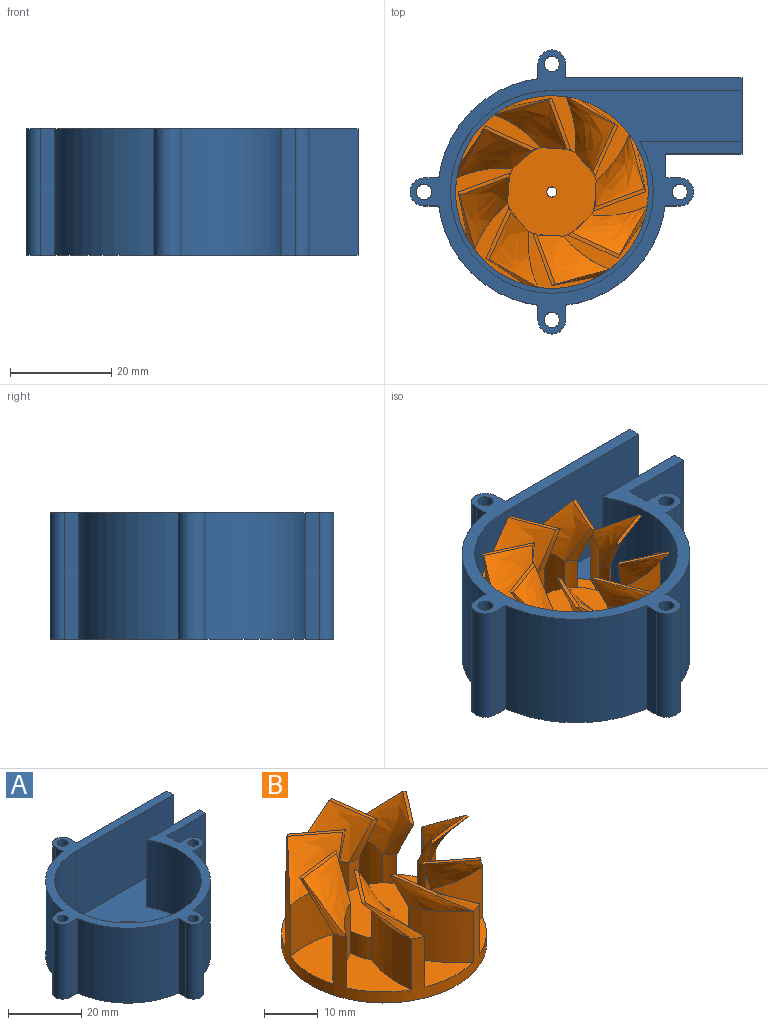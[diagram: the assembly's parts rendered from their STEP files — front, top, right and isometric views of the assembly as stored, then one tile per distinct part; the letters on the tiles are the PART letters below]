
ASSEMBLY  parts=2 mates=1
PART A: 34 faces, bbox 65.5x56x25 mm
  f0: plane 25x2.59mm, normal (0,1,0), area 64.7mm2, adj f1,f25,f26,f27
  f1: plane 25x4.75mm, normal (1,0,0), area 118.9mm2, adj f0,f2,f26,f27
  f2: plane 25x15mm, normal (0,-1,0), area 375mm2, adj f1,f6,f26,f27
  f3: plane 22.5x20.18mm, normal (0,1,0), area 454mm2, adj f4,f6,f26,f28
  f4: cylinder r=20mm len=40mm, axis (0,0,-1), area 2356.2mm2, adj f3,f5,f26,f28
  f5: plane 37.5x22.5mm, normal (0,-1,0), area 843.8mm2, adj f4,f6,f26,f28
  f6: plane 25x15mm, normal (1,0,0), area 150mm2, adj f2,f3,f5,f7,f26,f27,f28
  f7: plane 34.75x25mm, normal (0,1,0), area 868.9mm2, adj f6,f8,f26,f27
  f8: plane 25x2.59mm, normal (1,0,0), area 64.7mm2, adj f7,f9,f26,f27
  f9: cylinder r=2.75mm len=25mm, axis (0,0,-1), area 224mm2, adj f8,f10,f26,f27
  f10: plane 25x2.76mm, normal (-1,0,0), area 68.9mm2, adj f9,f11,f26,f27
  f11: cylinder r=22.5mm len=25mm, axis (0,0,-1), area 746mm2, adj f10,f12,f26,f27
  f12: plane 25x2.76mm, normal (0,1,0), area 68.9mm2, adj f11,f13,f26,f27
  f13: cylinder r=2.75mm len=25mm, axis (0,0,-1), area 224mm2, adj f12,f14,f26,f27
  f14: plane 25x2.76mm, normal (0,-1,0), area 68.9mm2, adj f13,f15,f26,f27
  f15: cylinder r=22.5mm len=25mm, axis (0,0,-1), area 746mm2, adj f14,f16,f26,f27
  f16: plane 25x2.76mm, normal (-1,0,0), area 68.9mm2, adj f15,f17,f26,f27
  f17: cylinder r=2.75mm len=25mm, axis (0,0,-1), area 224mm2, adj f16,f18,f26,f27
  f18: plane 25x2.76mm, normal (1,0,0), area 68.9mm2, adj f17,f19,f26,f27
  f19: cylinder r=22.5mm len=25mm, axis (0,0,-1), area 746mm2, adj f18,f20,f26,f27
  f20: plane 25x2.76mm, normal (0,-1,0), area 68.9mm2, adj f19,f25,f26,f27
  f21: cylinder r=1.5mm len=25mm, axis (0,0,-1), area 235.6mm2, adj f26,f27
  f22: cylinder r=1.5mm len=25mm, axis (0,0,-1), area 235.6mm2, adj f26,f27
  f23: cylinder r=1.5mm len=25mm, axis (0,0,-1), area 235.6mm2, adj f26,f27
  f24: cylinder r=1.5mm len=25mm, axis (0,0,-1), area 235.6mm2, adj f26,f27
  f25: cylinder r=2.75mm len=25mm, axis (0,0,-1), area 224mm2, adj f0,f20,f26,f27
  f26: plane 65.5x56mm, normal (0,0,1), area 495.8mm2, adj f0,f1,f2,f3,f4,f5,f6,f7
  f27: plane 65.5x56mm, normal (0,0,-1), area 1985mm2, adj f0,f1,f2,f6,f7,f8,f9,f10
  f28: plane 57.5x40mm, normal (0,0,1), area 1354.9mm2, adj f3,f4,f5,f6,f30
  f29: cylinder r=5mm len=10mm, axis (0,0,-1), area 125.7mm2, adj f31,f33
  f30: cylinder r=7mm len=14mm, axis (0,0,-1), area 175.9mm2, adj f28,f31
  f31: plane 14x14mm, normal (0,0,1), area 75.4mm2, adj f29,f30
  f32: cylinder r=2.5mm len=5mm, axis (0,0,-1), area 39.3mm2, adj f27,f33
  f33: plane 10x10mm, normal (0,0,1), area 58.9mm2, adj f29,f32
PART B: 88 faces, bbox 38x38x22 mm
  f0: cylinder r=9mm len=5mm, axis (0,0,-1), area 22.6mm2, adj f3,f19,f43,f47
  f1: plane 12.48x12.46mm, normal (0,0,1), area 84.3mm2, adj f14,f17,f26,f46
  f2: cylinder r=9mm len=5mm, axis (0,0,-1), area 22.6mm2, adj f5,f19,f40,f44
  f3: plane 16.31x9.64mm, normal (0,0,1), area 84.3mm2, adj f0,f17,f43,f47
  f4: cylinder r=9mm len=5mm, axis (0,0,-1), area 22.6mm2, adj f7,f19,f37,f41
  f5: plane 12.48x12.46mm, normal (0,0,1), area 84.3mm2, adj f2,f17,f40,f44
  f6: cylinder r=9mm len=5mm, axis (0,0,-1), area 22.6mm2, adj f9,f19,f34,f38
  f7: plane 16.31x9.64mm, normal (0,0,1), area 84.3mm2, adj f4,f17,f37,f41
  f8: cylinder r=9mm len=5mm, axis (0,0,-1), area 22.6mm2, adj f11,f19,f31,f35
  f9: plane 12.48x12.46mm, normal (0,0,1), area 84.3mm2, adj f6,f17,f34,f38
  f10: cylinder r=9mm len=5mm, axis (0,0,-1), area 22.6mm2, adj f13,f19,f28,f32
  f11: plane 16.31x9.64mm, normal (0,0,1), area 84.3mm2, adj f8,f17,f31,f35
  f12: cylinder r=9mm len=5mm, axis (0,0,-1), area 22.6mm2, adj f15,f19,f25,f29
  f13: plane 12.48x12.46mm, normal (0,0,1), area 84.3mm2, adj f10,f17,f28,f32
  f14: cylinder r=9mm len=5mm, axis (0,0,-1), area 22.6mm2, adj f1,f19,f26,f46
  f15: plane 16.31x9.64mm, normal (0,0,1), area 84.3mm2, adj f12,f17,f25,f29
  f16: cylinder r=7.5mm len=15mm, axis (0,0,-1), area 259.2mm2, adj f18,f20
  f17: cylinder r=19mm len=38mm, axis (0,0,-1), area 544.5mm2, adj f1,f3,f5,f7,f9,f11,f13,f15
  f18: plane 38x38mm, normal (0,0,-1), area 957.4mm2, adj f16,f17
  f19: plane 18x18mm, normal (0,0,1), area 251.3mm2, adj f0,f2,f4,f6,f8,f10,f12,f14
  f20: plane 15x15mm, normal (0,0,-1), area 113.1mm2, adj f16,f21
  f21: cylinder r=4.5mm len=9mm, axis (0,0,-1), area 155.5mm2, adj f20,f22
  f22: plane 9x9mm, normal (0,0,-1), area 60.5mm2, adj f21,f23
  f23: cylinder r=1mm len=7.5mm, axis (0,0,-1), area 47.1mm2, adj f19,f22
  f24: cylinder r=9mm len=6.5mm, axis (0,0,-1), area 16.5mm2, adj f19,f25,f26,f69
  f25: cylinder r=20.82mm len=11.5mm, axis (0,0,-1), area 130.3mm2, adj f12,f15,f17,f24,f72
  f26: cylinder r=23mm len=11.5mm, axis (0,0,-1), area 140.9mm2, adj f1,f14,f17,f24,f70
  f27: cylinder r=9mm len=6.5mm, axis (0,0,-1), area 16.5mm2, adj f19,f28,f29,f64
  f28: cylinder r=20.82mm len=11.5mm, axis (0,0,-1), area 130.3mm2, adj f10,f13,f17,f27,f67
  f29: cylinder r=23mm len=12mm, axis (0,0,-1), area 140.9mm2, adj f12,f15,f17,f27,f65
  f30: cylinder r=9mm len=6.5mm, axis (0,0,-1), area 16.5mm2, adj f19,f31,f32,f59
  f31: cylinder r=20.82mm len=11.5mm, axis (0,0,-1), area 130.3mm2, adj f8,f11,f17,f30,f62
  f32: cylinder r=23mm len=11.5mm, axis (0,0,-1), area 140.9mm2, adj f10,f13,f17,f30,f60
  f33: cylinder r=9mm len=6.5mm, axis (0,0,-1), area 16.5mm2, adj f19,f34,f35,f54
  f34: cylinder r=20.82mm len=11.5mm, axis (0,0,-1), area 130.3mm2, adj f6,f9,f17,f33,f57
  f35: cylinder r=23mm len=12mm, axis (0,0,-1), area 140.9mm2, adj f8,f11,f17,f33,f55
  f36: cylinder r=9mm len=6.5mm, axis (0,0,-1), area 16.5mm2, adj f19,f37,f38,f52
  f37: cylinder r=20.82mm len=11.5mm, axis (0,0,-1), area 130.3mm2, adj f4,f7,f17,f36,f51
  f38: cylinder r=23mm len=11.5mm, axis (0,0,-1), area 140.9mm2, adj f6,f9,f17,f36,f49
  f39: cylinder r=9mm len=6.5mm, axis (0,0,-1), area 16.5mm2, adj f19,f40,f41,f84
  f40: cylinder r=20.82mm len=11.5mm, axis (0,0,-1), area 130.3mm2, adj f2,f5,f17,f39,f87
  f41: cylinder r=23mm len=12mm, axis (0,0,-1), area 140.9mm2, adj f4,f7,f17,f39,f85
  f42: cylinder r=9mm len=6.5mm, axis (0,0,-1), area 16.5mm2, adj f19,f43,f44,f79
  f43: cylinder r=20.82mm len=11.5mm, axis (0,0,-1), area 130.3mm2, adj f0,f3,f17,f42,f82
  f44: cylinder r=23mm len=11.5mm, axis (0,0,-1), area 140.9mm2, adj f2,f5,f17,f42,f80
  f45: cylinder r=9mm len=6.5mm, axis (0,0,-1), area 16.5mm2, adj f19,f46,f47,f74
  f46: cylinder r=20.82mm len=11.5mm, axis (0,0,-1), area 130.3mm2, adj f1,f14,f17,f45,f77
  f47: cylinder r=23mm len=12mm, axis (0,0,-1), area 140.9mm2, adj f0,f3,f17,f45,f75
  f48: plane 10.84x2.09mm, normal (0,0,1), area 7.4mm2, adj f49,f50,f51,f52
  f49: bspline ~11.17x10.61mm, area 105.8mm2, adj f38,f48,f50,f52
  f50: bspline ~11.73x8mm, area 14.3mm2, adj f17,f48,f49,f51
  f51: bspline ~12.36x10.23mm, area 108.2mm2, adj f37,f48,f50,f52
  f52: bspline ~8x5.76mm, area 13.7mm2, adj f36,f48,f49,f51
  f53: plane 9.08x6.85mm, normal (0,0,1), area 7.4mm2, adj f54,f55,f56,f57
  f54: bspline ~8x5.39mm, area 13.7mm2, adj f33,f53,f55,f57
  f55: bspline ~15.4x8mm, area 105.8mm2, adj f35,f53,f54,f56
  f56: bspline ~8.69x8mm, area 14.3mm2, adj f17,f53,f55,f57
  f57: bspline ~15.63x8.89mm, area 108.2mm2, adj f34,f53,f54,f56
  f58: plane 10.84x2.09mm, normal (0,0,1), area 7.4mm2, adj f59,f60,f61,f62
  f59: bspline ~8x5.76mm, area 13.7mm2, adj f30,f58,f60,f62
  f60: bspline ~11.17x10.61mm, area 105.8mm2, adj f32,f58,f59,f61
  f61: bspline ~11.73x8mm, area 14.3mm2, adj f17,f58,f60,f62
  f62: bspline ~12.36x10.23mm, area 108.2mm2, adj f31,f58,f59,f61
  f63: plane 9.08x6.85mm, normal (0,0,1), area 7.4mm2, adj f64,f65,f66,f67
  f64: bspline ~8x5.39mm, area 13.7mm2, adj f27,f63,f65,f67
  f65: bspline ~15.4x8mm, area 105.8mm2, adj f29,f63,f64,f66
  f66: bspline ~8.69x8mm, area 14.3mm2, adj f17,f63,f65,f67
  f67: bspline ~15.63x8.89mm, area 108.2mm2, adj f28,f63,f64,f66
  f68: plane 10.84x2.09mm, normal (0,0,1), area 7.4mm2, adj f69,f70,f71,f72
  f69: bspline ~8x5.76mm, area 13.7mm2, adj f24,f68,f70,f72
  f70: bspline ~11.17x10.61mm, area 105.8mm2, adj f26,f68,f69,f71
  f71: bspline ~11.73x8mm, area 14.3mm2, adj f17,f68,f70,f72
  f72: bspline ~12.36x10.23mm, area 108.2mm2, adj f25,f68,f69,f71
  f73: plane 9.08x6.85mm, normal (0,0,1), area 7.4mm2, adj f74,f75,f76,f77
  f74: bspline ~8x5.39mm, area 13.7mm2, adj f45,f73,f75,f77
  f75: bspline ~15.4x8mm, area 105.8mm2, adj f47,f73,f74,f76
  f76: bspline ~8.69x8mm, area 14.3mm2, adj f17,f73,f75,f77
  f77: bspline ~15.63x8.89mm, area 108.2mm2, adj f46,f73,f74,f76
  f78: plane 10.84x2.09mm, normal (0,0,1), area 7.4mm2, adj f79,f80,f81,f82
  f79: bspline ~8x5.76mm, area 13.7mm2, adj f42,f78,f80,f82
  f80: bspline ~11.17x10.61mm, area 105.8mm2, adj f44,f78,f79,f81
  f81: bspline ~11.73x8mm, area 14.3mm2, adj f17,f78,f80,f82
  f82: bspline ~12.36x10.23mm, area 108.2mm2, adj f43,f78,f79,f81
  f83: plane 9.08x6.85mm, normal (0,0,1), area 7.4mm2, adj f84,f85,f86,f87
  f84: bspline ~8x5.39mm, area 13.7mm2, adj f39,f83,f85,f87
  f85: bspline ~15.4x8mm, area 105.8mm2, adj f41,f83,f84,f86
  f86: bspline ~8.69x8mm, area 14.3mm2, adj f17,f83,f85,f87
  f87: bspline ~15.63x8.89mm, area 108.2mm2, adj f40,f83,f84,f86
PLACE A t=(12.14,15.57,7.72)mm
PLACE B rot(axis=(0,0,1),148deg) t=(12.14,15.57,10.67)mm
MATE cylindrical A.f29 <-> B.f0  axis (0,0,-1) through (12.14,15.57,10.22)mm
